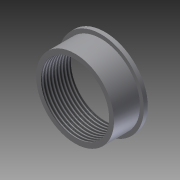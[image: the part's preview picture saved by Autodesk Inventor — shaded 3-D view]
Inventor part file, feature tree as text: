
AUTODESK INVENTOR PART (.ipt)
format: ipt  version: 2011 (Build 150239000, 239)  size: 98,816 bytes
history: native  units: in
note: dims shown in document units (in); Inventor stores cm internally (conversion verified against a paired STEP export)
features: extrude x3, sketch x3, thread x1
ambient origin geometry x8: Origin, YZ Plane, XZ Plane, XY Plane, X Axis, Y Axis, Z Axis, Center Point
bodies: Solid1 (feature_tree)
feature tree (7):
  extrude  "Extrusion1"  Depth=0.03in TaperAngle=0.0deg
  extrude  "Extrusion2"  Depth=0.2in TaperAngle=0.0deg
  extrude  "Extrusion3"  TaperAngle=0.0deg  [1 undecoded]
  thread  "Thread2"  [1 undecoded]
  sketch  "Sketch1"  dims[d0=0.66in d2=0.03in d3=0.0in]
  sketch  "Sketch3"  dims[d13=0.6in d14=0.2in d15=0.0in]
  sketch  "Sketch4"  dims[d16=0.525in d17=0.0in d18=0.0in d19=1.0in d20=0.0in]
note: 2 required parameter values undecoded (feature->parameter linkage not recoverable at this tier; creation-order binding heuristic only, values carry confidence <= 0.55)
